# Revit family: Crealco Skyline Standard Sash Top Hung E
name_source: partatom
category: Windows
revit_build: Autodesk Revit 2014 (Build: 20130308_1515(x64)
units: mm (PartAtom-declared; Revit-internal decimal feet)

## types (6) — shared parameters
Corrected Mullion Configuration = 2 mm  [stored 0.00656168 ft]
Custom Sash Height = 502 mm
Custom Sash Width = 502 mm
Custom Window Height = 890 mm  [stored 2.91995 ft]
Description = Top Hung Type E Standard Sash Window
Frame Profile Thickness = 41 mm  [stored 0.134514 ft]
Heavy Duty Sash = No
Limit Fixed Pane Height Max = 3000 mm  [stored 9.84252 ft]
Limit Fixed Pane Height Min = 200 mm  [stored 0.656168 ft]
Limit Fixed Pane Width Max = 3000 mm  [stored 9.84252 ft]
Limit Fixed Pane Width Min = 200 mm  [stored 0.656168 ft]
Limit Sash Height Max = 1200 mm  [stored 3.93701 ft]
Limit Sash Height Min = 300 mm  [stored 0.984252 ft]
Limit Sash Width Max = 1500 mm  [stored 4.92126 ft]
Limit Sash Width Min = 300 mm  [stored 0.984252 ft]
Manufacturer = Crealco
Max System DG Unit Thickness = 25 mm  [stored 0.082021 ft]
Model = Skyline
Rough Width = 3 mm  [stored 0.00984252 ft]
Sash Side Gap = 44 mm
Standard Mullion Different = No
Standard Sash = Yes
URL = www.crealco.co.za
Wall Closure = By host
zero-valued in all types: Custom Frame Offset From Exterior

## per-type parameters (varying)
| type | Clearvue Insulated LowE SHGC Value | Clearvue Insulated LowE U Value | Clearvue Insulated SHGC Value | Clearvue Insulated U Value | Clearvue SHGC Value | Clearvue U Value | Custom Windload | Custom Window Width | Energy Advantage SHGC Value | Energy Advantage U Value | Intruderprufe Insulated LowE SHGC Value | Intruderprufe Insulated LowE U Value | Intruderprufe Insulated SHGC Value | Intruderprufe Insulated U Value | Intruderprufe LowE SHGC Value | Intruderprufe LowE U Value | Intruderprufe SHGC Value | Intruderprufe U Value | Toughened Safety SHGC Value | Toughened Safety U Value |
| 1200 x 0900mm 1000Pa | 0.722 | 4.26 | 0.722 | 4.35 | 0.537 | 6.08 | 1000 mm  [stored 3.28084 ft] | 1190 mm  [stored 3.9042 ft] | 0.484 | 4.94 | 0.6 | 3.14 | 0.6 | 3.2 | 0.45 | 4.75 | 0.506 | 5.87 | 0.537 | 6.08 |
| 1200 x 0900mm 1500Pa | 0.722 | 4.26 | 0.722 | 4.35 | 0.537 | 6.08 | 1500 mm  [stored 4.92126 ft] | 1190 mm  [stored 3.9042 ft] | 0.484 | 4.94 | 0.6 | 3.14 | 0.6 | 3.2 | 0.45 | 4.75 | 0.506 | 5.87 | 0.537 | 6.08 |
| 1200 x 0900mm 2000Pa | 0.722 | 4.26 | 0.722 | 4.35 | 0.537 | 6.08 | 2000 mm  [stored 6.56168 ft] | 1190 mm  [stored 3.9042 ft] | 0.484 | 4.94 | 0.6 | 3.14 | 0.6 | 3.2 | 0.45 | 4.75 | 0.506 | 5.87 | 0.537 | 6.08 |
| 1500 x 0900mm 1000Pa | 0.748 | 4.42 | 0.748 | 4.49 | 0.579 | 6.06 | 1000 mm  [stored 3.28084 ft] | 1490 mm  [stored 4.88845 ft] | 0.52 | 4.77 | 0.621 | 3.13 | 0.621 | 3.18 | 0.484 | 4.6 | 0.454 | 5.85 | 0.579 | 6.06 |
| 1500 x 0900mm 1500Pa | 0.748 | 4.42 | 0.748 | 4.49 | 0.579 | 6.06 | 1500 mm  [stored 4.92126 ft] | 1490 mm  [stored 4.88845 ft] | 0.52 | 4.77 | 0.621 | 3.13 | 0.621 | 3.18 | 0.484 | 4.6 | 0.454 | 5.85 | 0.579 | 6.06 |
| 1500 x 0900mm 2000Pa | 0.748 | 4.42 | 0.748 | 4.49 | 0.579 | 6.06 | 2000 mm  [stored 6.56168 ft] | 1490 mm  [stored 4.88845 ft] | 0.52 | 4.77 | 0.621 | 3.13 | 0.621 | 3.18 | 0.484 | 4.6 | 0.454 | 5.85 | 0.579 | 6.06 |

note: [stored X ft] marks values corroborated as IEEE doubles in the binary element streams (Revit-internal decimal feet)

## geometry (parser evidence)
native form markers: Sweep x20
no freeform markers — native parametric forms only
